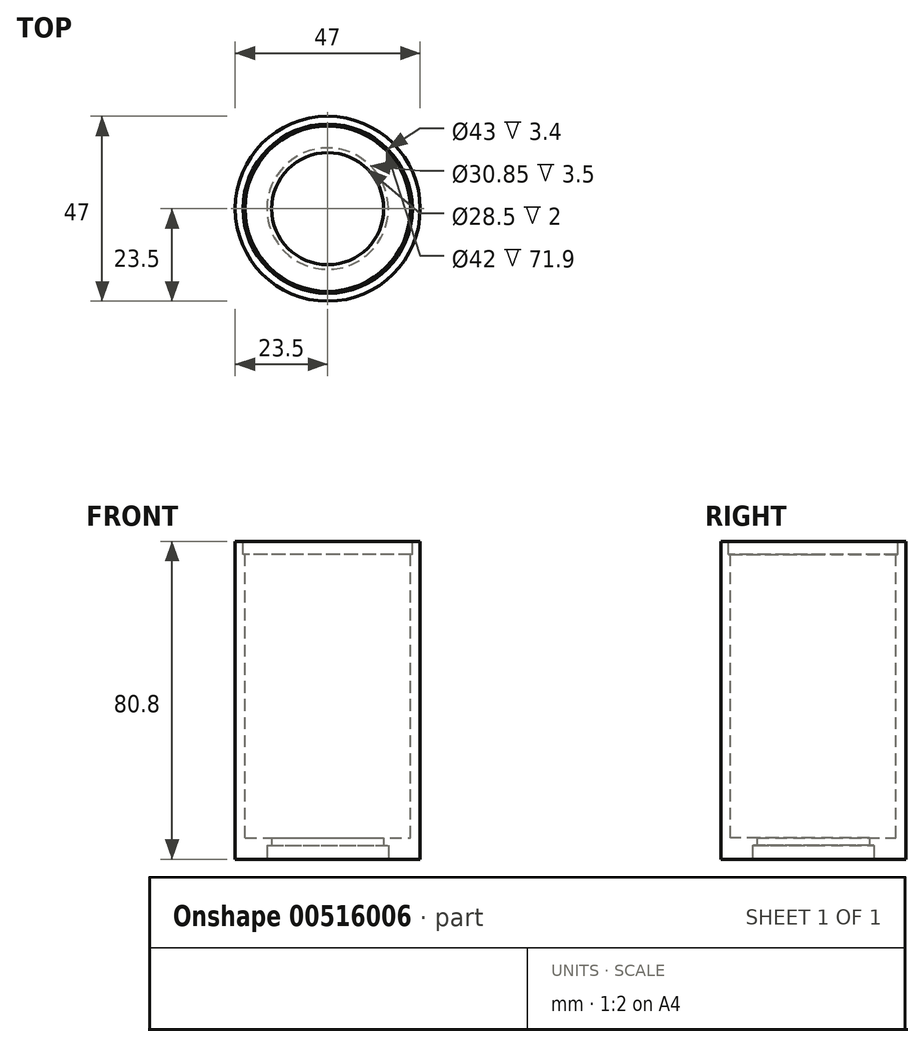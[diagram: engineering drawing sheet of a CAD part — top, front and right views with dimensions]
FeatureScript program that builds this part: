
annotation { "Feature Type Name" : "Feature", "Feature Type Description" : "" }
export const myFeature = defineFeature(function(context is Context, id is Id, definition is map)
    precondition{}
    {
        {
            var Q0;
            Q0=qCreatedBy(makeId("Top.planeOp"),FACE);
            var sketch = newSketch(context, id + "F0", { "sketchPlane" : qUnion([Q0])});
            skCircle(sketch, "E0", {"center": v(0, 0) * mm, "radius": 23.5 * mm});
            skSolve(sketch);
        }
        {
            var Q0;
            Q0=makeQuery(id+"F0.imprint","IMPRINT",FACE,{"disambiguationData":[TD([[makeQuery(id+"F0.imprint","IMPRINT",EDGE,{"derivedFrom":sQuery(id+"F0.wireOp",EDGE,"E0")}),1.0]])]});
            extrude(context, id + "F1", {"entities" : qUnion([Q0]), "depth" : (74 + 3.4 + 3.4) * mm, "offsetDistance" : 25 * mm});
        }
        {
            var Q0;
            Q0=makeQuery(id+"F1.opExtrude","CAP_FACE",FACE,{"disambiguationData":[OSD([sQuery(id+"F0.wireOp",EDGE,"E0")])],"isStart":false});
            var sketch = newSketch(context, id + "F2", { "sketchPlane" : qUnion([Q0])});
            skCircle(sketch, "E1", {"center": v(0, 0) * mm, "radius": 21.5 * mm});
            skSolve(sketch);
        }
        {
            var Q0;
            Q0=makeQuery(id+"F2.imprint","IMPRINT",FACE,{"disambiguationData":[TD([[makeQuery(id+"F2.imprint","IMPRINT",EDGE,{"derivedFrom":sQuery(id+"F2.wireOp",EDGE,"E1")}),1.0]])]});
            extrude(context, id + "F3", {"entities" : qUnion([Q0]), "operationType" : NewBodyOperationType.REMOVE, "oppositeDirection" : true, "depth" : 3.4 * mm, "offsetDistance" : 25 * mm});
        }
        {
            var Q0;
            Q0=makeQuery(id+"F3.boolean.opBoolean","COPY",FACE,{"derivedFrom":makeQuery(id+"F3.opExtrude","CAP_FACE",FACE,{"disambiguationData":[OSD([sQuery(id+"F2.wireOp",EDGE,"E1")])],"isStart":false})});
            var sketch = newSketch(context, id + "F4", { "sketchPlane" : qUnion([Q0])});
            skCircle(sketch, "E2", {"center": v(0, 0) * mm, "radius": 21 * mm});
            skSolve(sketch);
        }
        {
            var Q0;
            Q0=makeQuery(id+"F1.opExtrude","CAP_FACE",FACE,{"disambiguationData":[OSD([sQuery(id+"F0.wireOp",EDGE,"E0")])],"isStart":true});
            var sketch = newSketch(context, id + "F5", { "sketchPlane" : qUnion([Q0])});
            skCircle(sketch, "E3", {"center": v(0, 0) * mm, "radius": 15.43 * mm});
            skSolve(sketch);
        }
        {
            var Q0;
            Q0 = qSketchRegion(id + "F5", true);
            extrude(context, id + "F6", {"entities" : qUnion([Q0]), "operationType" : NewBodyOperationType.REMOVE, "oppositeDirection" : true, "depth" : 3.5 * mm, "offsetDistance" : 25 * mm});
        }
        {
            var Q0;
            Q0=makeQuery(id+"F6.boolean.opBoolean","COPY",FACE,{"derivedFrom":makeQuery(id+"F6.opExtrude","CAP_FACE",FACE,{"disambiguationData":[OSD([sQuery(id+"F5.wireOp",EDGE,"E3")])],"isStart":false})});
            var sketch = newSketch(context, id + "F7", { "sketchPlane" : qUnion([Q0])});
            skCircle(sketch, "E4", {"center": v(0, 0) * mm, "radius": 14.25 * mm});
            skSolve(sketch);
        }
        {
            var Q0;
            Q0 = qSketchRegion(id + "F7", true);
            extrude(context, id + "F8", {"entities" : qUnion([Q0]), "operationType" : NewBodyOperationType.REMOVE, "endBound" : BoundingType.THROUGH_ALL, "oppositeDirection" : true, "depth" : 50 * mm, "offsetDistance" : 25 * mm});
        }
        {
            var Q0;
            Q0 = qSketchRegion(id + "F4", true);
            var Q1;
            Q1=makeQuery(id+"F6.boolean.opBoolean","COPY",FACE,{"derivedFrom":makeQuery(id+"F6.opExtrude","CAP_FACE",FACE,{"disambiguationData":[OSD([sQuery(id+"F5.wireOp",EDGE,"E3")])],"isStart":false})});
            extrude(context, id + "F9", {"entities" : qUnion([Q0]), "operationType" : NewBodyOperationType.REMOVE, "endBound" : BoundingType.UP_TO_SURFACE, "oppositeDirection" : true, "depth" : 25 * mm, "endBoundEntityFace" : qUnion([Q1]), "hasOffset" : true, "offsetDistance" : 2 * mm});
        }
    });
